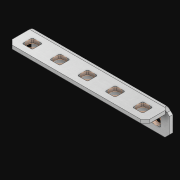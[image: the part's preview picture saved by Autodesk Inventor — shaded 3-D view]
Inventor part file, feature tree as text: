
AUTODESK INVENTOR PART (.ipt)
format: ipt  version: 2021 (Build 250183000, 183)  size: 563,200 bytes
history: native  units: in
note: dims shown in document units (in); Inventor stores cm internally (conversion verified against a paired STEP export)
features: extrude x11, other x10, sketch x3, pattern_linear x1, sheet_metal_op x1
ambient origin geometry x8: Origin, YZ Plane, XZ Plane, XY Plane, X Axis, Y Axis, Z Axis, Center Point
bodies: Solid1 (feature_tree)
feature tree (26):
  pattern_linear  "Rectangular Pattern1"  Spacing1=0.063in  [1 undecoded]
  extrude  "Extrusion1"  Depth=0.5in
  sketch  "Sketch1"  dims[d0=0.182in]
  other  "Srf1"
  sketch  "Sketch2"  dims[d1=0.063in d2=0.0in]
  other  "Srf2"
  other  "Srf3"
  other  "Srf5"
  other  "Srf7"
  other  "Srf9"
  other  "Srf4"
  other  "Srf6"
  other  "Srf8"
  other  "Srf10"
  sketch  "Sketch3"  dims[d3=0.182in d4=0.063in d5=0.0in d8=0.5in d9=15.0in d10=0.0in]
  sheet_metal_op  "Fold1"
  extrude  "ExtrusionSrf1"  Depth=0.5in TaperAngle=0.0deg
  extrude  "ExtrusionSrf2"  [1 undecoded]
  extrude  "ExtrusionSrf3"  [1 undecoded]
  extrude  "ExtrusionSrf4"  [1 undecoded]
  extrude  "ExtrusionSrf5"  [1 undecoded]
  extrude  "ExtrusionSrf6"  [1 undecoded]
  extrude  "ExtrusionSrf37"  [1 undecoded]
  extrude  "ExtrusionSrf38"  [1 undecoded]
  extrude  "ExtrusionSrf39"  [1 undecoded]
  extrude  "ExtrusionSrf40"  [1 undecoded]
note: 10 required parameter values undecoded (feature->parameter linkage not recoverable at this tier; creation-order binding heuristic only, values carry confidence <= 0.55)
